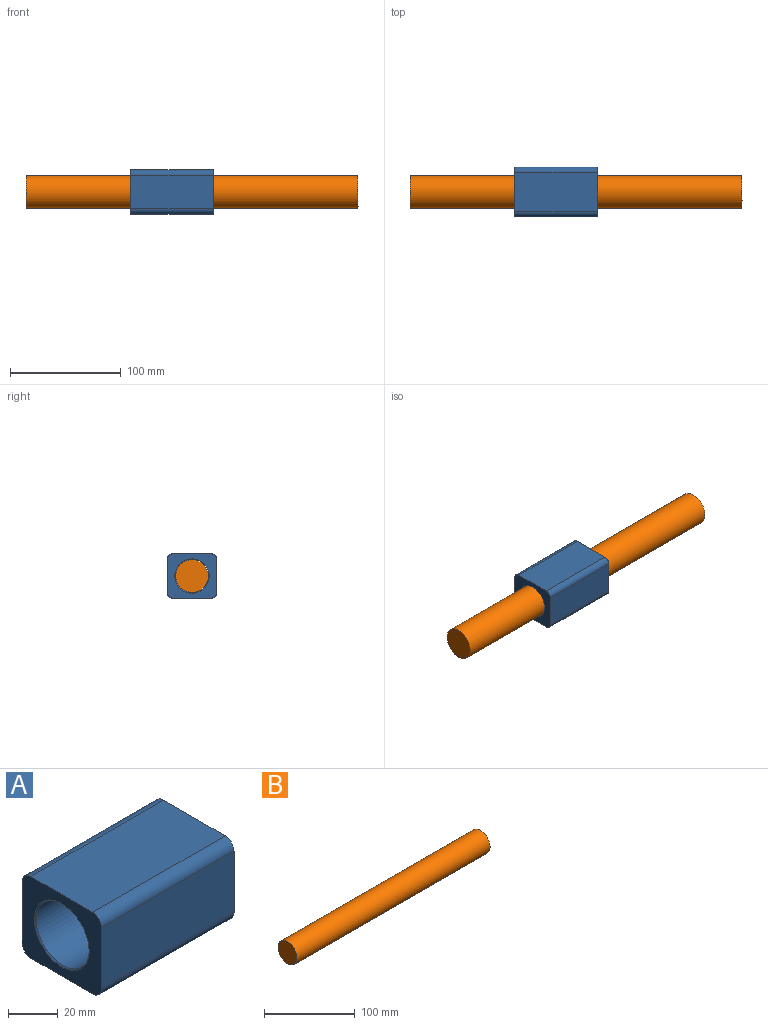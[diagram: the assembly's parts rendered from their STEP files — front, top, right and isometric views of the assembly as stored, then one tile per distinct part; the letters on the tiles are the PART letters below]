
ASSEMBLY  parts=2 mates=1
PART A: 13 faces, bbox 75x45x40 mm
  f0: plane 75x30mm, normal (0,1,0), area 2250mm2, adj f5,f6,f9,f12
  f1: plane 75x35mm, normal (0,0,1), area 2625mm2, adj f5,f6,f9,f10
  f2: plane 75x30mm, normal (0,-1,0), area 2250mm2, adj f5,f6,f10,f11
  f3: cylinder r=15mm len=74mm, axis (1,0,0), area 6974.3mm2, adj f7,f8
  f4: plane 75x35mm, normal (0,0,-1), area 2625mm2, adj f5,f6,f11,f12
  f5: plane 45x40mm, normal (-1,0,0), area 1023.8mm2, adj f0,f1,f2,f4,f7,f9,f10,f11
  f6: plane 45x40mm, normal (1,0,0), area 1023.8mm2, adj f0,f1,f2,f4,f8,f9,f10,f11
  f7: cone r=15.5mm half-angle=45deg, axis (-1,0,0), area 67.8mm2, adj f3,f5
  f8: cone r=15mm half-angle=45deg, axis (1,0,0), area 67.8mm2, adj f3,f6
  f9: cylinder r=5mm len=75mm, axis (-1,0,0), area 589mm2, adj f0,f1,f5,f6
  f10: cylinder r=5mm len=75mm, axis (-1,0,0), area 589mm2, adj f1,f2,f5,f6
  f11: cylinder r=5mm len=75mm, axis (1,0,0), area 589mm2, adj f2,f4,f5,f6
  f12: cylinder r=5mm len=75mm, axis (1,0,0), area 589mm2, adj f0,f4,f5,f6
PART B: 3 faces, bbox 300x29.5x29.5 mm
  f0: cylinder r=14.75mm len=300mm, axis (-1,0,0), area 27803.1mm2, adj f1,f2
  f1: plane 29.5x29.5mm, normal (1,0,0), area 683.5mm2, adj f0
  f2: plane 29.5x29.5mm, normal (-1,0,0), area 683.5mm2, adj f0
PLACE A t=(231.67,119.32,-85.25)mm fixed
PLACE B t=(212.21,119.32,-85.25)mm
MATE slider B.f0 <-> A.f3  axis (-1,0,0) through (399.71,119.32,34.75)mm
